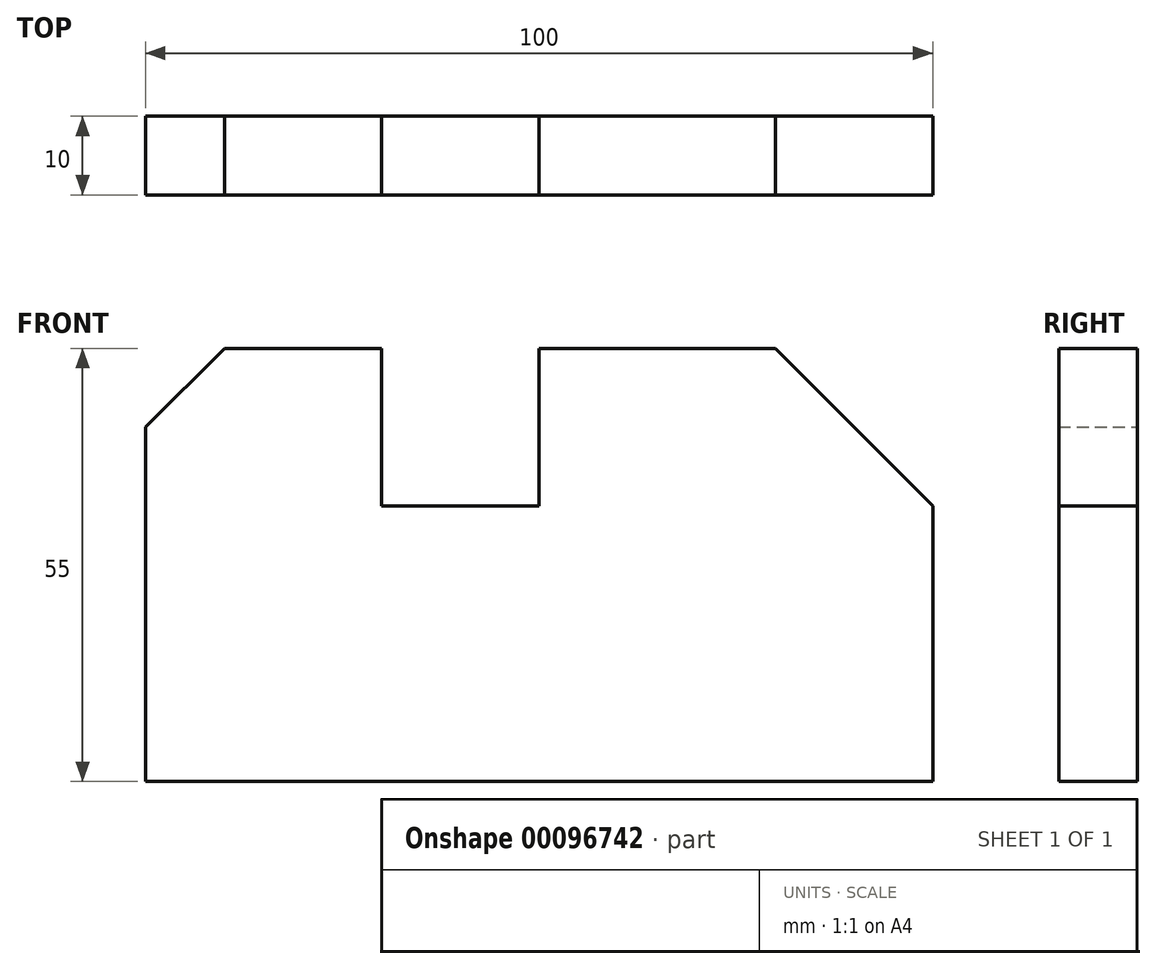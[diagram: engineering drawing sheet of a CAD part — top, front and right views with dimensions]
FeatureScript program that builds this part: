
annotation { "Feature Type Name" : "Feature", "Feature Type Description" : "" }
export const myFeature = defineFeature(function(context is Context, id is Id, definition is map)
    precondition{}
    {
        {
            var Q0;
            Q0=qCreatedBy(makeId("Front.planeOp"),FACE);
            var sketch = newSketch(context, id + "F0", { "sketchPlane" : qUnion([Q0])});
            skLineSegment(sketch, "E0", {"start": v(0, 0) * mm, "end": v(100, 0) * mm});
            skLineSegment(sketch, "E1", {"start": v(0, 0) * mm, "end": v(0, 45) * mm});
            skLineSegment(sketch, "E2", {"start": v(100, 0) * mm, "end": v(100, 35) * mm});
            skLineSegment(sketch, "E3", {"start": v(30, 55) * mm, "end": v(30, 35) * mm});
            skLineSegment(sketch, "E4", {"start": v(30, 35) * mm, "end": v(50, 35) * mm});
            skLineSegment(sketch, "E5", {"start": v(50, 35) * mm, "end": v(50, 55) * mm});
            skLineSegment(sketch, "E6", {"start": v(50, 55) * mm, "end": v(80, 55) * mm});
            skLineSegment(sketch, "E7", {"start": v(80, 55) * mm, "end": v(100, 35) * mm});
            skLineSegment(sketch, "E8", {"start": v(10, 55) * mm, "end": v(0, 45) * mm});
            skLineSegment(sketch, "E9", {"start": v(10, 55) * mm, "end": v(30, 55) * mm});
            skSolve(sketch);
        }
        {
            var Q0;
            Q0 = qSketchRegion(id + "F0", true);
            extrude(context, id + "F1", {"entities" : qUnion([Q0]), "depth" : 10 * mm});
        }
    });
